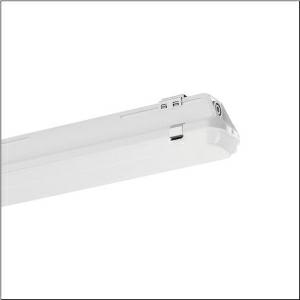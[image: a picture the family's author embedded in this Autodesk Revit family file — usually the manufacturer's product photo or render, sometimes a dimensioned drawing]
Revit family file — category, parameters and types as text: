
# Revit family: monsun_r__21_51fb107p660c_cadc
name_source: partatom
category: Lighting Fixtures
units: mm (PartAtom-declared; Revit-internal decimal feet)

## family parameters
Cut with Voids When Loaded = No
Host = Face
Light Source = No
Part Type = Normal
Room Calculation Point = No
Round Connector Dimension = Use Diameter
Shared = No

## types (1)
- Monsun® 21 (1 x LED, 6010 lm, 34.9 W, 6500K)
    Apparent Load = 35 VA
    CIE Flux Codes = 47 77 93 94 100
    Color Rendering = 80
    Color Temperature = 6500K
    Default Elevation = 1800 mm
    Description = Monsun® 21, damp-proof luminaire, chain hanger, primary optical cover: enclosure, of PMMA, light emission: direct distribution, primary light characteristic: symmetric, installation type: suspended mounting, surface-mounted, horizontal mounting, vertical mounting, LED, rated luminous flux: 6.010lm, luminous efficacy: 172lm/W, light colour: 865, colour temperature: 6500K, control gear: ON/OFF, with terminal, 3-pole, max. 2.5mm², mains connection: 220..240V, AC, 50/60Hz, rated input power: 35W, housing, of glass-fibre reinforced polyester, uncoated, bright grey, incl. chain hanger, length: 1.590mm, width: 90mm, height: 88mm, clip for enclosure, of stainless steel (V2A), ceiling mounting element, of stainless steel (V2A), chain hanger, of stainless steel (V2A), protection rating (complete): IP66, insulation class (complete): insulation class I (protective earthing), certification: CE, ENEC, VDE, UKCA, protection symbol: D, impact resistance: IK04, permissible operating ambient temperature: -25..+35°C, standard: EN 50419, EN 60598-2-1, corresponds to IFS (International Featured Standards) requirements for safety and quality in the food industry, for indoor or canopied outdoor use, no direct snow, no direct sun, no direct rain, LABS conformity tested according to VDMA 24364:2018-05, contact your sales advisor before using the luminaires in applications with unclear chemical exposure, large temperature fluctuations or condensation-forming humidity, packaging unit: 1 piece
    Height = 89 mm
    Lamp = 1 x LED
    Lamp Light Flux = 6010 lm
    Lamp Power = 34.9 W
    Lamp count = 1
    Length = 1590 mm
    Luminous efficacy = 172 lm/W
    Manufacturer = Siteco
    ModVariant = No
    Model = 51FB107P660C
    Mounting Place = Ceiling
    Mounting Type = Surface mounted
    Number of Poles = 1
    OnlyDefault = Yes
    Power Factor = 1
    Product Name = Monsun® 21
    Product group = damp-proof luminaire
    ProductGroupID = 300
    Protection Class = Protection class I
    Protection Degree = IP 66
    RLX_Detail_Level = 1
    RLX_Emergency_Light_Flux = 0 lm
    RLX_Emergency_Type = 0
    RLX_Emergency_Type_DB = No
    RlxData = <blob elided: 88593 chars, md5=d0a2930c>
    Socket = socket
    Standby Power = 0 W
    System Light Flux = 6010 lm
    System Power = 35 W
    Type Comments = Product without accessories
    Type Image = l_1319656.jpg
    URL = http://relux.com
    VarID = ---
    Voltage = 0 V
    Weight = 0.00 kg
    Width = 90 mm

## geometry (parser evidence)
native form markers: Blend x4, Sweep x14
no freeform markers — native parametric forms only
